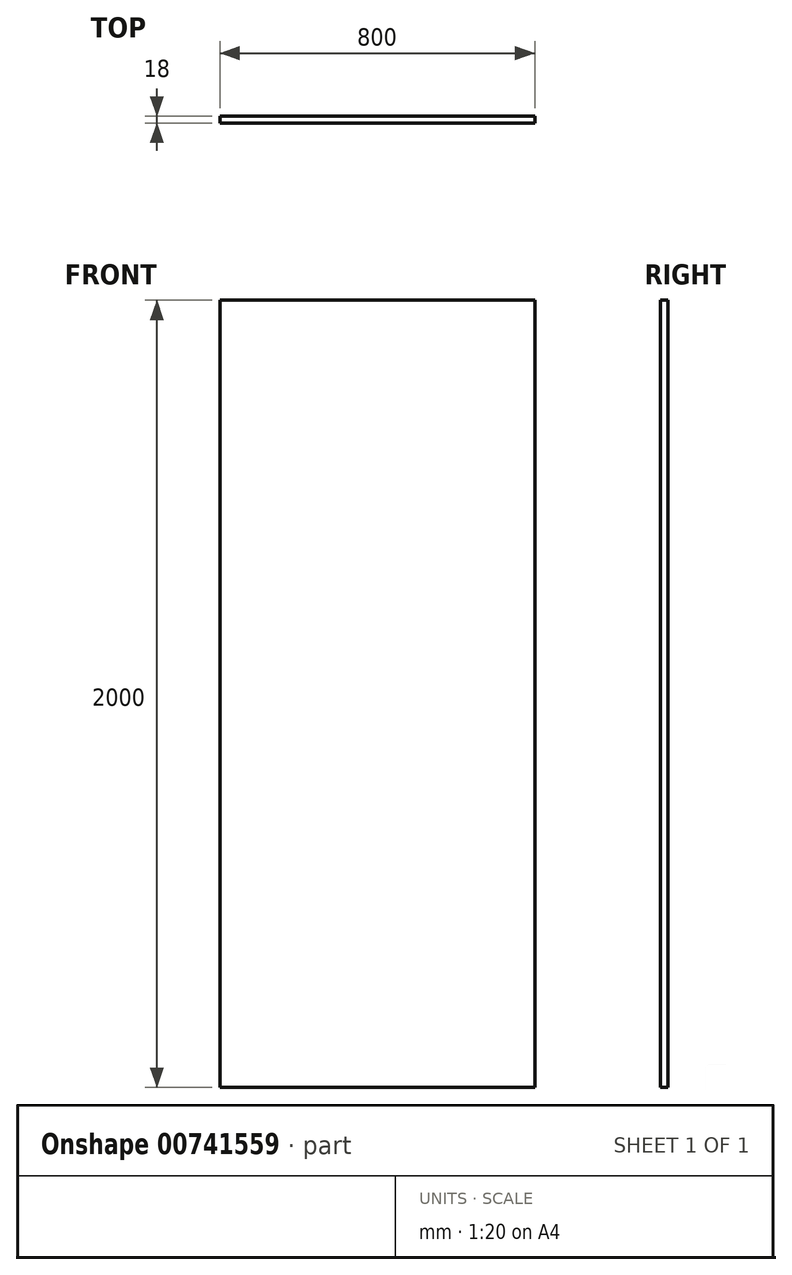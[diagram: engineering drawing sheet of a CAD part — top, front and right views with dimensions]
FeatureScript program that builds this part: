
annotation { "Feature Type Name" : "Feature", "Feature Type Description" : "" }
export const myFeature = defineFeature(function(context is Context, id is Id, definition is map)
    precondition{}
    {
        {
            var Q0;
            Q0=qCreatedBy(makeId("Front.planeOp"),FACE);
            var sketch = newSketch(context, id + "F0", { "sketchPlane" : qUnion([Q0])});
            skLineSegment(sketch, "E0.bottom", {"start": v(-400, -1000) * mm, "end": v(400, -1000) * mm});
            skLineSegment(sketch, "E0.top", {"start": v(-400, 1000) * mm, "end": v(400, 1000) * mm});
            skLineSegment(sketch, "E0.left", {"start": v(-400, -1000) * mm, "end": v(-400, 1000) * mm});
            skLineSegment(sketch, "E0.right", {"start": v(400, -1000) * mm, "end": v(400, 1000) * mm});
            skPoint(sketch, "E0.middle", {"position": v(0, 0) * mm});
            skSolve(sketch);
        }
        {
            var Q0;
            Q0=qSketchRegion(id+"F0",true);
            extrude(context, id + "F1", {"entities" : qUnion([Q0]), "oppositeDirection" : true, "depth" : 18 * mm, "offsetDistance" : 25 * mm});
        }
    });
